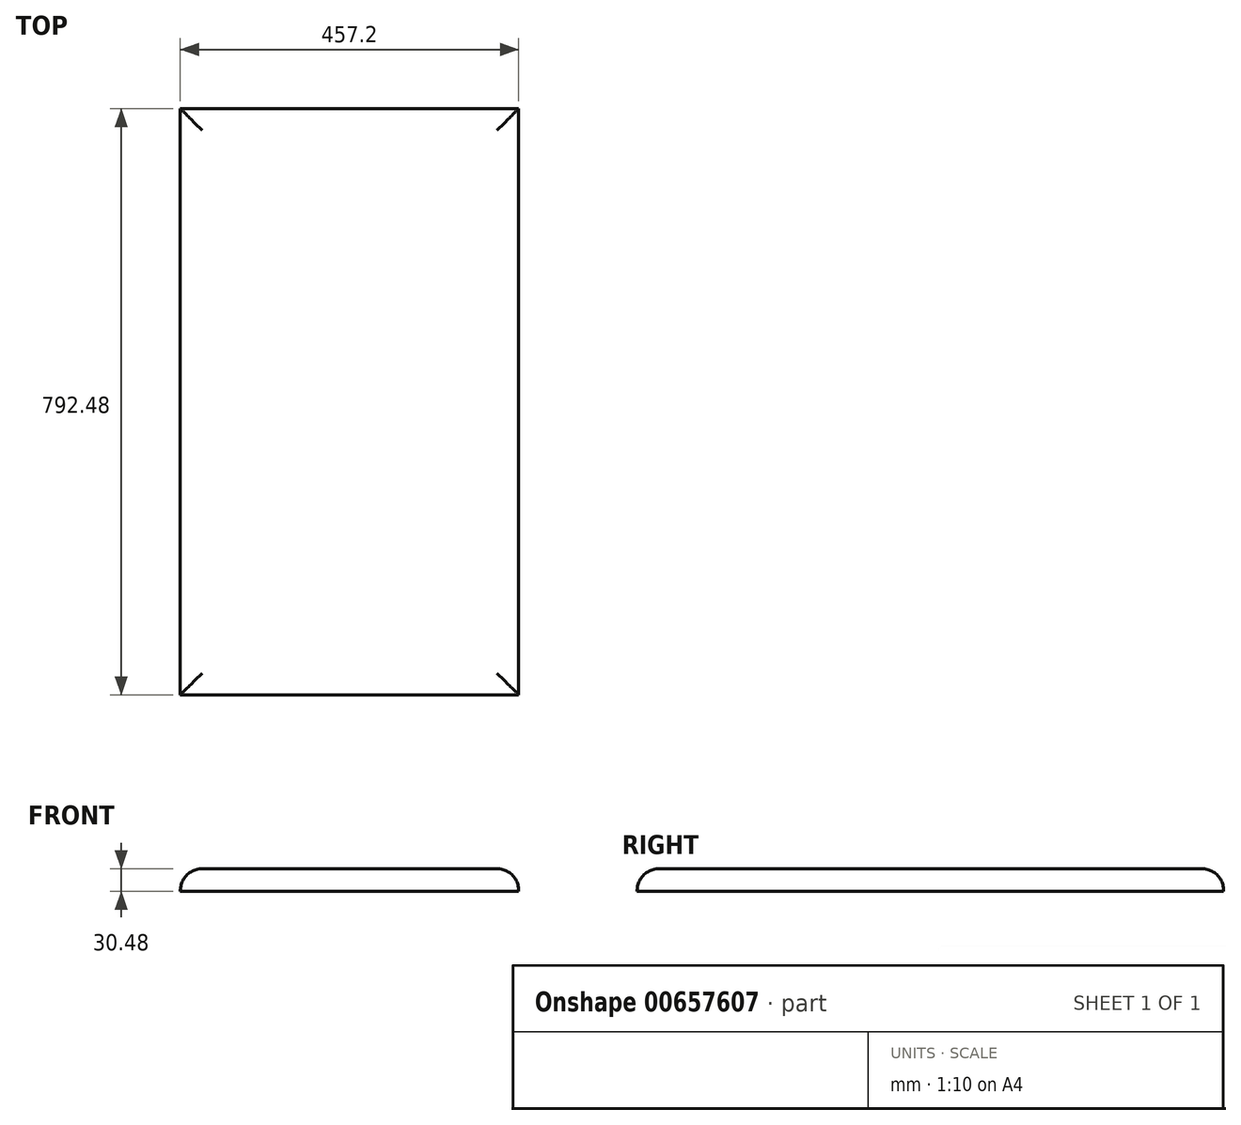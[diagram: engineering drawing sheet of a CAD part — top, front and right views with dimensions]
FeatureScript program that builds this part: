
annotation { "Feature Type Name" : "Feature", "Feature Type Description" : "" }
export const myFeature = defineFeature(function(context is Context, id is Id, definition is map)
    precondition{}
    {
        {
            var Q0;
            Q0=qCreatedBy(makeId("Top.planeOp"),FACE);
            var sketch = newSketch(context, id + "F0", { "sketchPlane" : qUnion([Q0])});
            skLineSegment(sketch, "E0.bottom", {"start": v(-235.12, 545.29) * mm, "end": v(222.08, 545.29) * mm});
            skLineSegment(sketch, "E0.top", {"start": v(-235.12, -247.2) * mm, "end": v(222.08, -247.2) * mm});
            skLineSegment(sketch, "E0.left", {"start": v(-235.12, 545.29) * mm, "end": v(-235.12, -247.2) * mm});
            skLineSegment(sketch, "E0.right", {"start": v(222.08, 545.29) * mm, "end": v(222.08, -247.2) * mm});
            skSolve(sketch);
        }
        {
            var Q0;
            Q0=makeQuery(id+"F0.imprint","IMPRINT",FACE,{"disambiguationData":[TD([[makeQuery(id+"F0.imprint","IMPRINT",EDGE,{"derivedFrom":sQuery(id+"F0.wireOp",EDGE,"E0.bottom")}),-1.0]])]});
            extrude(context, id + "F1", {"entities" : qUnion([Q0]), "depth" : 30.48 * mm, "offsetDistance" : 30.48 * mm});
        }
        {
            var Q0;
            Q0=makeQuery(id+"F1.opExtrude","CAP_EDGE",EDGE,{"disambiguationData":[OSD([sQuery(id+"F0.wireOp",EDGE,"E0.left")])],"isStart":false});
            var Q1;
            Q1=makeQuery(id+"F1.opExtrude","CAP_EDGE",EDGE,{"disambiguationData":[OSD([sQuery(id+"F0.wireOp",EDGE,"E0.top")])],"isStart":false});
            var Q2;
            Q2=makeQuery(id+"F1.opExtrude","CAP_EDGE",EDGE,{"disambiguationData":[OSD([sQuery(id+"F0.wireOp",EDGE,"E0.right")])],"isStart":false});
            var Q3;
            Q3=makeQuery(id+"F1.opExtrude","CAP_EDGE",EDGE,{"disambiguationData":[OSD([sQuery(id+"F0.wireOp",EDGE,"E0.bottom")])],"isStart":false});
            fillet(context, id + "F2", {"entities" : qUnion([Q0, Q1, Q2, Q3]), "radius" : 29.43 * mm, "tangentPropagation" : true, "allowEdgeOverflow" : false});
        }
    });
